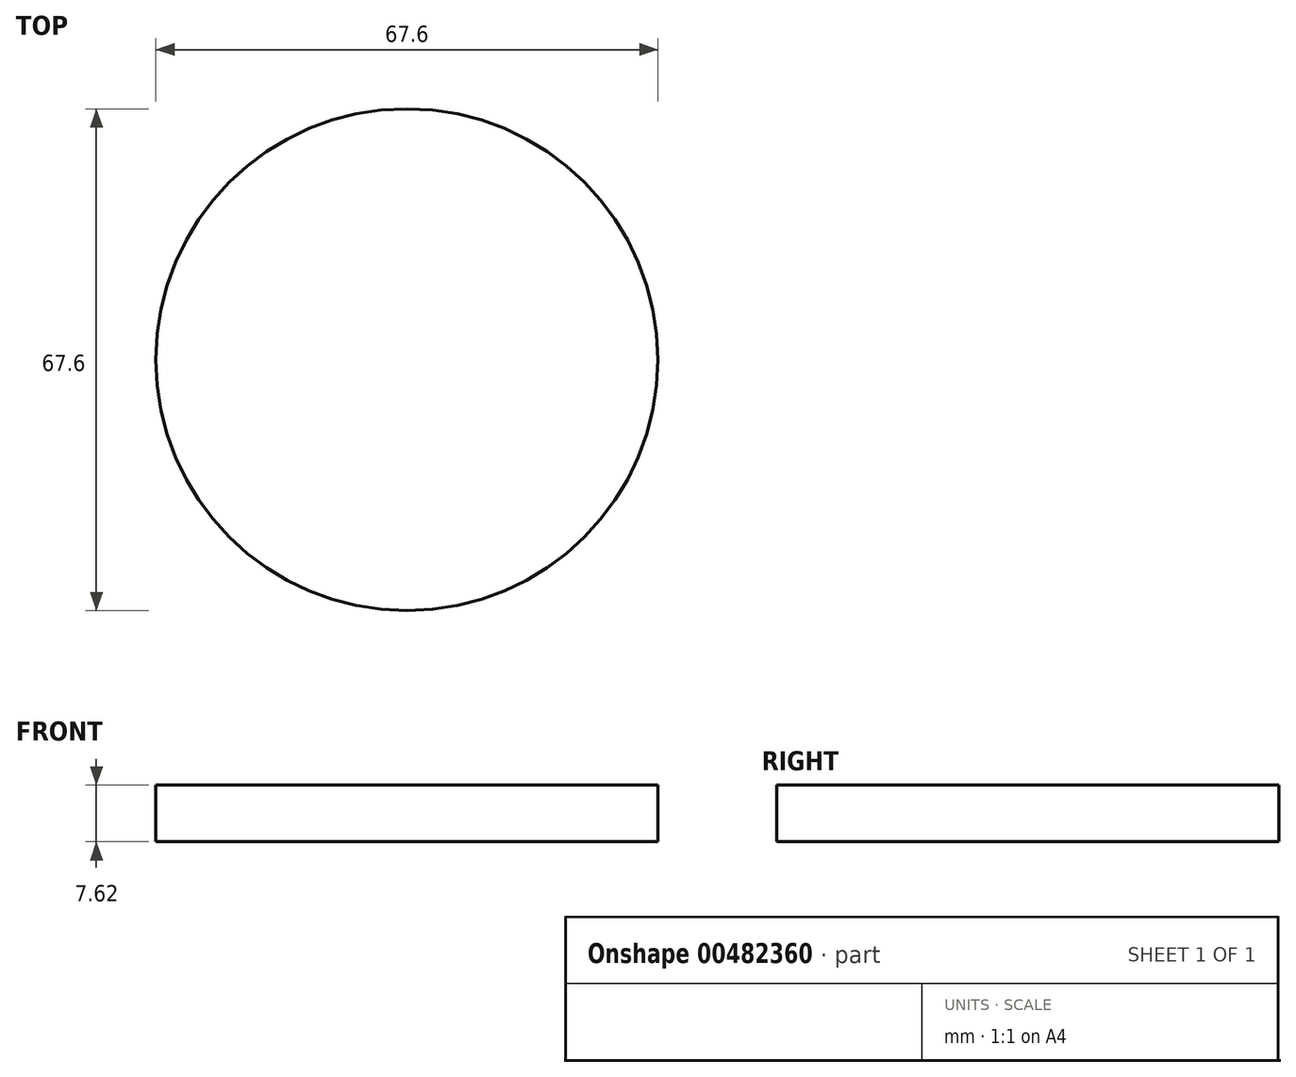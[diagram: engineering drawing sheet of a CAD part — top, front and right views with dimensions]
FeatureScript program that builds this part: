
annotation { "Feature Type Name" : "Feature", "Feature Type Description" : "" }
export const myFeature = defineFeature(function(context is Context, id is Id, definition is map)
    precondition{}
    {
        {
            var Q0;
            Q0=qCreatedBy(makeId("Top.planeOp"),FACE);
            var sketch = newSketch(context, id + "F0", { "sketchPlane" : qUnion([Q0])});
            skCircle(sketch, "E0", {"center": v(-130.47, 73.46) * mm, "radius": 33.8 * mm});
            skSolve(sketch);
        }
        {
            var Q0;
            Q0 = qSketchRegion(id + "F0", true);
            extrude(context, id + "F1", {"entities" : qUnion([Q0]), "depth" : 7.62 * mm});
        }
    });
